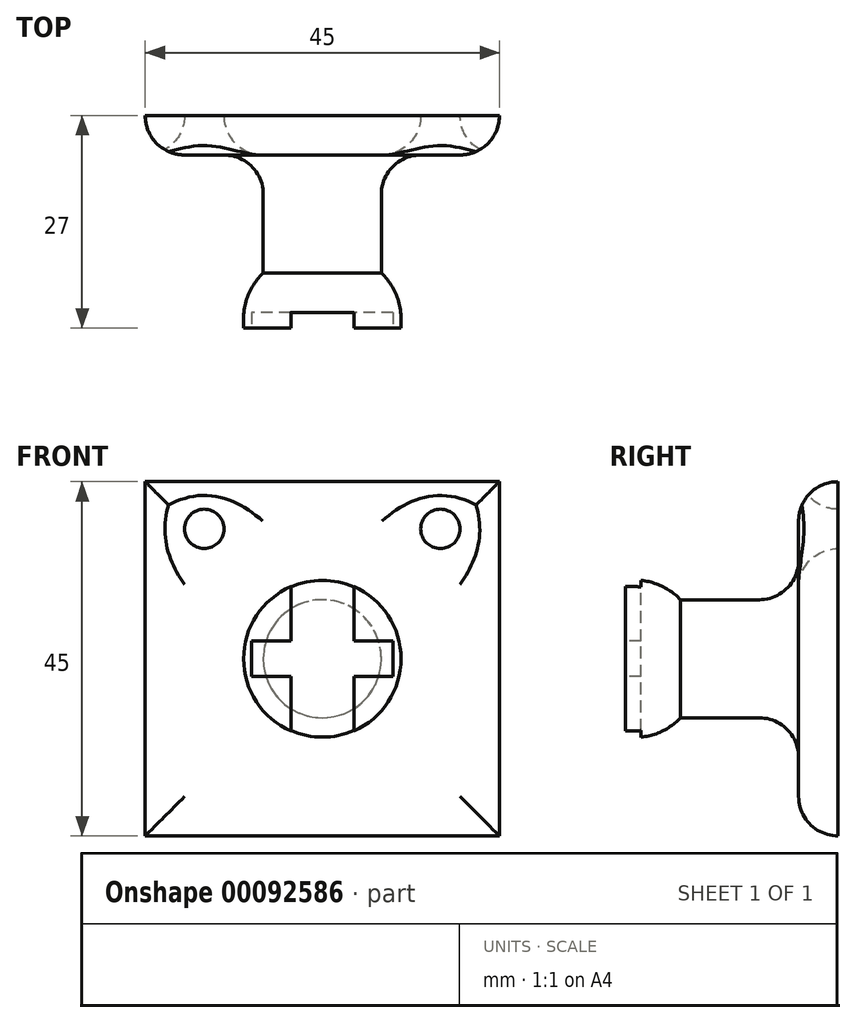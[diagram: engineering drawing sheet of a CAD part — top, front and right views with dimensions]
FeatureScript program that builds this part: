
annotation { "Feature Type Name" : "Feature", "Feature Type Description" : "" }
export const myFeature = defineFeature(function(context is Context, id is Id, definition is map)
    precondition{}
    {
        {
            var Q0;
            Q0=qCreatedBy(makeId("Front.planeOp"),FACE);
            var sketch = newSketch(context, id + "F0", { "sketchPlane" : qUnion([Q0])});
            skLineSegment(sketch, "E0", {"start": v(-25.32, 13.99) * mm, "end": v(-25.32, -31.01) * mm});
            skLineSegment(sketch, "E1", {"start": v(-25.32, -31.01) * mm, "end": v(19.68, -31.01) * mm});
            skLineSegment(sketch, "E2", {"start": v(19.68, -31.01) * mm, "end": v(19.68, 13.99) * mm});
            skLineSegment(sketch, "E3", {"start": v(19.68, 13.99) * mm, "end": v(-25.32, 13.99) * mm});
            skCircle(sketch, "E4", {"center": v(-2.82, -8.51) * mm, "radius": 7.5 * mm});
            skSolve(sketch);
        }
        {
            var Q0;
            Q0=makeQuery(id+"F0.imprint","IMPRINT",FACE,{"disambiguationData":[TD([[makeQuery(id+"F0.imprint","IMPRINT",EDGE,{"derivedFrom":sQuery(id+"F0.wireOp",EDGE,"E4")}),1.0]])]});
            extrude(context, id + "F1", {"entities" : qUnion([Q0]), "depth" : 20 * mm});
        }
        {
            var Q0;
            Q0=qSketchRegion(id+"F0",true);
            extrude(context, id + "F2", {"entities" : qUnion([Q0]), "operationType" : NewBodyOperationType.ADD, "depth" : 5 * mm});
        }
        {
            var Q0;
            Q0=makeQuery(id+"F2.opExtrude","CAP_FACE",FACE,{"disambiguationData":[OSD([sQuery(id+"F0.wireOp",EDGE,"E0"),sQuery(id+"F0.wireOp",EDGE,"E1"),sQuery(id+"F0.wireOp",EDGE,"E2"),sQuery(id+"F0.wireOp",EDGE,"E3"),sQuery(id+"F0.wireOp",EDGE,"E4")])],"isStart":false});
            var sketch = newSketch(context, id + "F3", { "sketchPlane" : qUnion([Q0])});
            skCircle(sketch, "E5", {"center": v(-17.82, 7.99) * mm, "radius": 2.5 * mm});
            skCircle(sketch, "E6", {"center": v(12.18, 7.99) * mm, "radius": 2.5 * mm});
            skSolve(sketch);
        }
        {
            var Q0;
            Q0=makeQuery(id+"F3.imprint","IMPRINT",FACE,{"disambiguationData":[TD([[makeQuery(id+"F3.imprint","IMPRINT",EDGE,{"derivedFrom":sQuery(id+"F3.wireOp",EDGE,"E6")}),1.0]])]});
            var Q1;
            Q1=makeQuery(id+"F3.imprint","IMPRINT",FACE,{"disambiguationData":[TD([[makeQuery(id+"F3.imprint","IMPRINT",EDGE,{"derivedFrom":sQuery(id+"F3.wireOp",EDGE,"E5")}),1.0]])]});
            extrude(context, id + "F4", {"entities" : qUnion([Q0, Q1]), "operationType" : NewBodyOperationType.REMOVE, "oppositeDirection" : true, "depth" : 25 * mm});
        }
        {
            var Q0;
            Q0=makeQuery(id+"F1.opExtrude","CAP_FACE",FACE,{"disambiguationData":[OSD([sQuery(id+"F0.wireOp",EDGE,"E4")])],"isStart":false});
            var sketch = newSketch(context, id + "F5", { "sketchPlane" : qUnion([Q0])});
            skCircle(sketch, "E7", {"center": v(-2.82, -8.51) * mm, "radius": 10 * mm});
            skSolve(sketch);
        }
        {
            var Q0;
            Q0=makeQuery(id+"F5.imprint","IMPRINT",FACE,{"disambiguationData":[TD([[makeQuery(id+"F5.imprint","IMPRINT",EDGE,{"derivedFrom":makeQuery(id+"F1.opExtrude","CAP_EDGE",EDGE,{"disambiguationData":[OSD([sQuery(id+"F0.wireOp",EDGE,"E4")])],"isStart":false})}),1.0]])]});
            var Q1;
            Q1=makeQuery(id+"F5.imprint","IMPRINT",FACE,{"disambiguationData":[TD([[makeQuery(id+"F5.imprint","IMPRINT",EDGE,{"derivedFrom":sQuery(id+"F5.wireOp",EDGE,"E7")}),1.0]])]});
            extrude(context, id + "F6", {"entities" : qUnion([Q0, Q1]), "operationType" : NewBodyOperationType.ADD, "depth" : 7 * mm});
        }
        {
            var Q0;
            Q0=makeQuery(id+"F6.opExtrude","CAP_FACE",FACE,{"disambiguationData":[OSD([sQuery(id+"F5.wireOp",EDGE,"E7")])],"isStart":false});
            var sketch = newSketch(context, id + "F7", { "sketchPlane" : qUnion([Q0])});
            skLineSegment(sketch, "E8.bottom", {"start": v(-6.82, -20.53) * mm, "end": v(1.18, -20.53) * mm});
            skLineSegment(sketch, "E8.top", {"start": v(-6.82, 3.5) * mm, "end": v(1.18, 3.5) * mm});
            skLineSegment(sketch, "E8.left", {"start": v(-6.82, -20.53) * mm, "end": v(-6.82, 3.5) * mm});
            skLineSegment(sketch, "E8.right", {"start": v(1.18, -20.53) * mm, "end": v(1.18, 3.5) * mm});
            skPoint(sketch, "E8.middle", {"position": v(-2.82, -8.51) * mm});
            skLineSegment(sketch, "E9.bottom", {"start": v(6.18, -10.76) * mm, "end": v(-11.82, -10.76) * mm});
            skLineSegment(sketch, "E9.top", {"start": v(6.18, -6.26) * mm, "end": v(-11.82, -6.26) * mm});
            skLineSegment(sketch, "E9.left", {"start": v(6.18, -10.76) * mm, "end": v(6.18, -6.26) * mm});
            skLineSegment(sketch, "E9.right", {"start": v(-11.82, -10.76) * mm, "end": v(-11.82, -6.26) * mm});
            skSolve(sketch);
        }
        {
            var Q0;
            Q0 = qSketchRegion(id + "F7", true);
            extrude(context, id + "F8", {"entities" : qUnion([Q0]), "operationType" : NewBodyOperationType.REMOVE, "oppositeDirection" : true, "depth" : 2 * mm});
        }
        {
            var Q0;
            Q0=makeQuery(id+"F2.opExtrude","CAP_FACE",FACE,{"disambiguationData":[OSD([sQuery(id+"F0.wireOp",EDGE,"E0"),sQuery(id+"F0.wireOp",EDGE,"E1"),sQuery(id+"F0.wireOp",EDGE,"E2"),sQuery(id+"F0.wireOp",EDGE,"E3"),sQuery(id+"F0.wireOp",EDGE,"E4")])],"isStart":false});
            fillet(context, id + "F9", {"entities" : qUnion([Q0]), "radius" : 5 * mm, "tangentPropagation" : true, "allowEdgeOverflow" : false});
        }
        {
            var Q0;
            Q0=makeQuery(id+"F6.opExtrude","CAP_EDGE",EDGE,{"disambiguationData":[OSD([sQuery(id+"F5.wireOp",EDGE,"E7")])],"isStart":true});
            fillet(context, id + "F10", {"entities" : qUnion([Q0]), "radius" : 8 * mm, "tangentPropagation" : true, "allowEdgeOverflow" : false});
        }
    });
